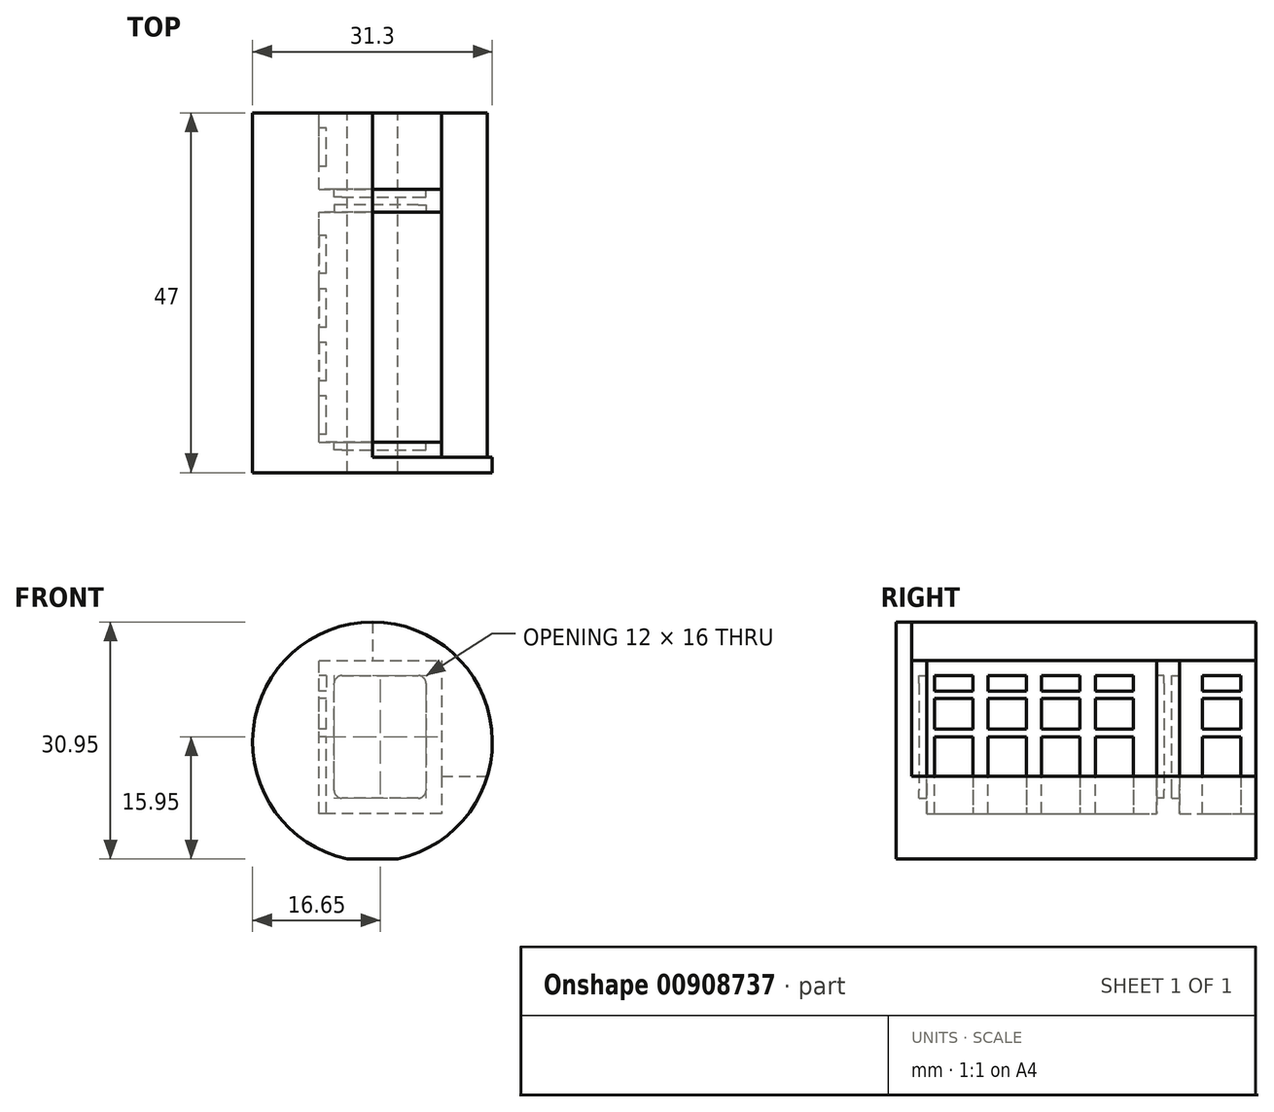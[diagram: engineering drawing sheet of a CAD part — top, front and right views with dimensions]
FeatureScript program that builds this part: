
annotation { "Feature Type Name" : "Feature", "Feature Type Description" : "" }
export const myFeature = defineFeature(function(context is Context, id is Id, definition is map)
    precondition{}
    {
        {
            var Q0;
            Q0=qCreatedBy(makeId("Front.planeOp"),FACE);
            var sketch = newSketch(context, id + "F0", { "sketchPlane" : qUnion([Q0])});
            skArc(sketch, "E0", {"start": v(3.3, 0) * mm, "mid": v(0, 30.95) * mm, "end": v(-3.3, 0) * mm});
            skLineSegment(sketch, "E1", {"start": v(3.3, 0) * mm, "end": v(-3.3, 0) * mm});
            skSolve(sketch);
        }
        {
            var Q0;
            Q0 = qSketchRegion(id + "F0", true);
            extrude(context, id + "F1", {"entities" : qUnion([Q0]), "depth" : 47 * mm, "offsetDistance" : 25 * mm});
        }
        {
            var Q0;
            Q0=makeQuery(id+"F1.opExtrude","CAP_FACE",FACE,{"disambiguationData":[OSD([sQuery(id+"F0.wireOp",EDGE,"E0"),sQuery(id+"F0.wireOp",EDGE,"E1")])],"isStart":true});
            var sketch = newSketch(context, id + "F2", { "sketchPlane" : qUnion([Q0])});
            skLineSegment(sketch, "E2", {"start": v(0, 30.95) * mm, "end": v(0, 25.95) * mm});
            skLineSegment(sketch, "E3", {"start": v(0, 25.95) * mm, "end": v(7, 25.95) * mm});
            skLineSegment(sketch, "E4", {"start": v(7, 25.95) * mm, "end": v(7, 5.95) * mm});
            skLineSegment(sketch, "E5", {"start": v(7, 5.95) * mm, "end": v(-9, 5.95) * mm});
            skLineSegment(sketch, "E6", {"start": v(-9, 5.95) * mm, "end": v(-9, 10.84) * mm});
            skLineSegment(sketch, "E7", {"start": v(-9, 10.84) * mm, "end": v(-15, 10.84) * mm});
            skArc(sketch, "E8.0", {"start": v(-15, 10.84) * mm, "mid": v(-12.55, 24.66) * mm, "end": v(0, 30.95) * mm});
            skPoint(sketch, "E9.orphan", {"position": v(3.3, 0) * mm});
            skPoint(sketch, "E10.orphan", {"position": v(-3.3, 0) * mm});
            skSolve(sketch);
        }
        {
            var Q0;
            Q0 = qSketchRegion(id + "F2", true);
            extrude(context, id + "F3", {"entities" : qUnion([Q0]), "operationType" : NewBodyOperationType.REMOVE, "oppositeDirection" : true, "depth" : 45 * mm, "offsetDistance" : 25 * mm});
        }
        {
            var Q0;
            Q0=makeQuery(id+"F3.boolean.opBoolean","COPY",FACE,{"derivedFrom":makeQuery(id+"F3.opExtrude","CAP_FACE",FACE,{"disambiguationData":[OSD([sQuery(id+"F2.wireOp",EDGE,"E2"),sQuery(id+"F2.wireOp",EDGE,"E3"),sQuery(id+"F2.wireOp",EDGE,"E4"),sQuery(id+"F2.wireOp",EDGE,"E5"),sQuery(id+"F2.wireOp",EDGE,"E6"),sQuery(id+"F2.wireOp",EDGE,"E7"),sQuery(id+"F2.wireOp",EDGE,"E8.0")])],"isStart":false})});
            var sketch = newSketch(context, id + "F4", { "sketchPlane" : qUnion([Q0])});
            skLineSegment(sketch, "E11", {"start": v(-9, 10.84) * mm, "end": v(-9, 25.95) * mm});
            skLineSegment(sketch, "E12", {"start": v(-9, 25.95) * mm, "end": v(0, 25.95) * mm});
            skLineSegment(sketch, "E13.0", {"start": v(7, 5.95) * mm, "end": v(-9, 5.95) * mm});
            skPoint(sketch, "E14.0", {"position": v(-9, 8.4) * mm});
            skLineSegment(sketch, "E15.0", {"start": v(-9, 5.95) * mm, "end": v(-9, 10.84) * mm});
            skLineSegment(sketch, "E16.0", {"start": v(0, 25.95) * mm, "end": v(7, 25.95) * mm});
            skLineSegment(sketch, "E17.0", {"start": v(7, 25.95) * mm, "end": v(7, 5.95) * mm});
            skSolve(sketch);
        }
        {
            var Q0;
            Q0=makeQuery(id+"F4.imprint","IMPRINT",FACE,{"disambiguationData":[TD([[makeQuery(id+"F4.imprint","IMPRINT",EDGE,{"derivedFrom":sQuery(id+"F4.wireOp",EDGE,"E11")}),-1.0]])]});
            extrude(context, id + "F5", {"entities" : qUnion([Q0]), "operationType" : NewBodyOperationType.ADD, "depth" : 2 * mm, "offsetDistance" : 25 * mm});
        }
        {
            var Q0;
            Q0=makeQuery(id+"F5.opExtrude","CAP_FACE",FACE,{"disambiguationData":[OSD([sQuery(id+"F4.wireOp",EDGE,"E11"),sQuery(id+"F4.wireOp",EDGE,"E12"),sQuery(id+"F4.wireOp",EDGE,"E13.0"),sQuery(id+"F4.wireOp",EDGE,"E15.0"),sQuery(id+"F4.wireOp",EDGE,"E16.0"),sQuery(id+"F4.wireOp",EDGE,"E17.0")])],"isStart":false});
            var sketch = newSketch(context, id + "F6", { "sketchPlane" : qUnion([Q0])});
            skLineSegment(sketch, "E18.0", {"start": v(-7, 23.95) * mm, "end": v(-7, 7.95) * mm});
            skLineSegment(sketch, "E18.1", {"start": v(0, 23.95) * mm, "end": v(-7, 23.95) * mm});
            skLineSegment(sketch, "E18.2", {"start": v(-7, 7.95) * mm, "end": v(5, 7.95) * mm});
            skLineSegment(sketch, "E18.3", {"start": v(5, 7.95) * mm, "end": v(5, 23.95) * mm});
            skLineSegment(sketch, "E18.4", {"start": v(5, 23.95) * mm, "end": v(0, 23.95) * mm});
            skSolve(sketch);
        }
        {
            var Q0;
            Q0 = qSketchRegion(id + "F6", true);
            extrude(context, id + "F7", {"entities" : qUnion([Q0]), "operationType" : NewBodyOperationType.REMOVE, "oppositeDirection" : true, "depth" : 1 * mm, "offsetDistance" : 25 * mm});
        }
        {
            var Q0;
            Q0=makeQuery(id+"F7.boolean.opBoolean","COPY",EDGE,{"derivedFrom":makeQuery(id+"F7.opExtrude","SWEPT_EDGE",EDGE,{"disambiguationData":[OSD([sQuery(id+"F6.wireOp",EDGE,"E18.0"),sQuery(id+"F6.wireOp",EDGE,"E18.1")])]})});
            var Q1;
            Q1=makeQuery(id+"F7.boolean.opBoolean","COPY",EDGE,{"derivedFrom":makeQuery(id+"F7.opExtrude","SWEPT_EDGE",EDGE,{"disambiguationData":[OSD([sQuery(id+"F6.wireOp",EDGE,"E18.3"),sQuery(id+"F6.wireOp",EDGE,"E18.4")])]})});
            var Q2;
            Q2=makeQuery(id+"F7.boolean.opBoolean","COPY",EDGE,{"derivedFrom":makeQuery(id+"F7.opExtrude","SWEPT_EDGE",EDGE,{"disambiguationData":[OSD([sQuery(id+"F6.wireOp",EDGE,"E18.0"),sQuery(id+"F6.wireOp",EDGE,"E18.2")])]})});
            var Q3;
            Q3=makeQuery(id+"F7.boolean.opBoolean","COPY",EDGE,{"derivedFrom":makeQuery(id+"F7.opExtrude","SWEPT_EDGE",EDGE,{"disambiguationData":[OSD([sQuery(id+"F6.wireOp",EDGE,"E18.2"),sQuery(id+"F6.wireOp",EDGE,"E18.3")])]})});
            fillet(context, id + "F8", {"entities" : qUnion([Q0, Q1, Q2, Q3]), "radius" : 1 * mm, "tangentPropagation" : true, "allowEdgeOverflow" : false});
        }
        {
            var Q0;
            Q0=makeQuery(id+"F3.boolean.opBoolean","COPY",FACE,{"derivedFrom":makeQuery(id+"F3.opExtrude","SWEPT_FACE",FACE,{"disambiguationData":[OSD([sQuery(id+"F2.wireOp",EDGE,"E4")])]})});
            var sketch = newSketch(context, id + "F9", { "sketchPlane" : qUnion([Q0])});
            skLineSegment(sketch, "E19", {"start": v(-42, 5.95) * mm, "end": v(-37, 5.95) * mm});
            skLineSegment(sketch, "E20", {"start": v(-42, 5.95) * mm, "end": v(-42, 15.95) * mm});
            skLineSegment(sketch, "E21", {"start": v(-42, 15.95) * mm, "end": v(-37, 15.95) * mm});
            skLineSegment(sketch, "E22", {"start": v(-37, 15.95) * mm, "end": v(-37, 5.95) * mm});
            skLineSegment(sketch, "E23.bottom", {"start": v(-42, 16.95) * mm, "end": v(-37, 16.95) * mm});
            skLineSegment(sketch, "E23.top", {"start": v(-42, 20.95) * mm, "end": v(-37, 20.95) * mm});
            skLineSegment(sketch, "E23.left", {"start": v(-42, 16.95) * mm, "end": v(-42, 20.95) * mm});
            skLineSegment(sketch, "E23.right", {"start": v(-37, 16.95) * mm, "end": v(-37, 20.95) * mm});
            skLineSegment(sketch, "E24", {"start": v(-42, 21.95) * mm, "end": v(-37, 21.95) * mm});
            skLineSegment(sketch, "E25", {"start": v(-37, 21.95) * mm, "end": v(-37, 23.95) * mm});
            skLineSegment(sketch, "E26", {"start": v(-37, 23.95) * mm, "end": v(-42, 23.95) * mm});
            skLineSegment(sketch, "E27", {"start": v(-42, 23.95) * mm, "end": v(-42, 21.95) * mm});
            skLineSegment(sketch, "E28.1.0.0", {"start": v(-30, 23.95) * mm, "end": v(-35, 23.95) * mm});
            skLineSegment(sketch, "E28.1.0.1", {"start": v(-35, 23.95) * mm, "end": v(-35, 21.95) * mm});
            skLineSegment(sketch, "E28.1.0.2", {"start": v(-35, 21.95) * mm, "end": v(-30, 21.95) * mm});
            skLineSegment(sketch, "E28.1.0.3", {"start": v(-30, 21.95) * mm, "end": v(-30, 23.95) * mm});
            skLineSegment(sketch, "E28.1.0.4", {"start": v(-35, 20.95) * mm, "end": v(-30, 20.95) * mm});
            skLineSegment(sketch, "E28.1.0.5", {"start": v(-35, 16.95) * mm, "end": v(-35, 20.95) * mm});
            skLineSegment(sketch, "E28.1.0.6", {"start": v(-30, 16.95) * mm, "end": v(-30, 20.95) * mm});
            skLineSegment(sketch, "E28.1.0.7", {"start": v(-35, 16.95) * mm, "end": v(-30, 16.95) * mm});
            skLineSegment(sketch, "E28.1.0.8", {"start": v(-35, 15.95) * mm, "end": v(-30, 15.95) * mm});
            skLineSegment(sketch, "E28.1.0.9", {"start": v(-35, 5.95) * mm, "end": v(-35, 15.95) * mm});
            skLineSegment(sketch, "E28.1.0.10", {"start": v(-35, 5.95) * mm, "end": v(-30, 5.95) * mm});
            skLineSegment(sketch, "E28.1.0.11", {"start": v(-30, 15.95) * mm, "end": v(-30, 5.95) * mm});
            skLineSegment(sketch, "E28.2.0.0", {"start": v(-23, 23.95) * mm, "end": v(-28, 23.95) * mm});
            skLineSegment(sketch, "E28.2.0.1", {"start": v(-28, 23.95) * mm, "end": v(-28, 21.95) * mm});
            skLineSegment(sketch, "E28.2.0.2", {"start": v(-28, 21.95) * mm, "end": v(-23, 21.95) * mm});
            skLineSegment(sketch, "E28.2.0.3", {"start": v(-23, 21.95) * mm, "end": v(-23, 23.95) * mm});
            skLineSegment(sketch, "E28.2.0.4", {"start": v(-28, 20.95) * mm, "end": v(-23, 20.95) * mm});
            skLineSegment(sketch, "E28.2.0.5", {"start": v(-28, 16.95) * mm, "end": v(-28, 20.95) * mm});
            skLineSegment(sketch, "E28.2.0.6", {"start": v(-23, 16.95) * mm, "end": v(-23, 20.95) * mm});
            skLineSegment(sketch, "E28.2.0.7", {"start": v(-28, 16.95) * mm, "end": v(-23, 16.95) * mm});
            skLineSegment(sketch, "E28.2.0.8", {"start": v(-28, 15.95) * mm, "end": v(-23, 15.95) * mm});
            skLineSegment(sketch, "E28.2.0.9", {"start": v(-28, 5.95) * mm, "end": v(-28, 15.95) * mm});
            skLineSegment(sketch, "E28.2.0.10", {"start": v(-28, 5.95) * mm, "end": v(-23, 5.95) * mm});
            skLineSegment(sketch, "E28.2.0.11", {"start": v(-23, 15.95) * mm, "end": v(-23, 5.95) * mm});
            skLineSegment(sketch, "E28.3.0.0", {"start": v(-16, 23.95) * mm, "end": v(-21, 23.95) * mm});
            skLineSegment(sketch, "E28.3.0.1", {"start": v(-21, 23.95) * mm, "end": v(-21, 21.95) * mm});
            skLineSegment(sketch, "E28.3.0.2", {"start": v(-21, 21.95) * mm, "end": v(-16, 21.95) * mm});
            skLineSegment(sketch, "E28.3.0.3", {"start": v(-16, 21.95) * mm, "end": v(-16, 23.95) * mm});
            skLineSegment(sketch, "E28.3.0.4", {"start": v(-21, 20.95) * mm, "end": v(-16, 20.95) * mm});
            skLineSegment(sketch, "E28.3.0.5", {"start": v(-21, 16.95) * mm, "end": v(-21, 20.95) * mm});
            skLineSegment(sketch, "E28.3.0.6", {"start": v(-16, 16.95) * mm, "end": v(-16, 20.95) * mm});
            skLineSegment(sketch, "E28.3.0.7", {"start": v(-21, 16.95) * mm, "end": v(-16, 16.95) * mm});
            skLineSegment(sketch, "E28.3.0.8", {"start": v(-21, 15.95) * mm, "end": v(-16, 15.95) * mm});
            skLineSegment(sketch, "E28.3.0.9", {"start": v(-21, 5.95) * mm, "end": v(-21, 15.95) * mm});
            skLineSegment(sketch, "E28.3.0.10", {"start": v(-21, 5.95) * mm, "end": v(-16, 5.95) * mm});
            skLineSegment(sketch, "E28.3.0.11", {"start": v(-16, 15.95) * mm, "end": v(-16, 5.95) * mm});
            skLineSegment(sketch, "E28.direction1", {"start": v(-42, 23.95) * mm, "end": v(-35, 23.95) * mm, "construction": true});
            skLineSegment(sketch, "E29.1.0.0", {"start": v(-7, 21.95) * mm, "end": v(-2, 21.95) * mm});
            skLineSegment(sketch, "E29.1.0.1", {"start": v(-2, 23.95) * mm, "end": v(-7, 23.95) * mm});
            skLineSegment(sketch, "E29.1.0.2", {"start": v(-7, 23.95) * mm, "end": v(-7, 21.95) * mm});
            skLineSegment(sketch, "E29.1.0.3", {"start": v(-2, 21.95) * mm, "end": v(-2, 23.95) * mm});
            skLineSegment(sketch, "E29.1.0.4", {"start": v(-7, 20.95) * mm, "end": v(-2, 20.95) * mm});
            skLineSegment(sketch, "E29.1.0.5", {"start": v(-7, 16.95) * mm, "end": v(-7, 20.95) * mm});
            skLineSegment(sketch, "E29.1.0.6", {"start": v(-7, 16.95) * mm, "end": v(-2, 16.95) * mm});
            skLineSegment(sketch, "E29.1.0.7", {"start": v(-2, 16.95) * mm, "end": v(-2, 20.95) * mm});
            skLineSegment(sketch, "E29.1.0.8", {"start": v(-7, 15.95) * mm, "end": v(-2, 15.95) * mm});
            skLineSegment(sketch, "E29.1.0.9", {"start": v(-7, 5.95) * mm, "end": v(-7, 15.95) * mm});
            skLineSegment(sketch, "E29.1.0.10", {"start": v(-7, 5.95) * mm, "end": v(-2, 5.95) * mm});
            skLineSegment(sketch, "E29.1.0.11", {"start": v(-2, 15.95) * mm, "end": v(-2, 5.95) * mm});
            skLineSegment(sketch, "E29.direction1", {"start": v(-21, 21.95) * mm, "end": v(-7, 21.95) * mm, "construction": true});
            skSolve(sketch);
        }
        {
            var Q0;
            Q0 = qSketchRegion(id + "F9", true);
            extrude(context, id + "F10", {"entities" : qUnion([Q0]), "operationType" : NewBodyOperationType.ADD, "depth" : 1 * mm, "offsetDistance" : 25 * mm});
        }
        {
            var Q0;
            Q0=makeQuery(id+"F5.opExtrude","CAP_FACE",FACE,{"disambiguationData":[OSD([sQuery(id+"F4.wireOp",EDGE,"E11"),sQuery(id+"F4.wireOp",EDGE,"E12"),sQuery(id+"F4.wireOp",EDGE,"E13.0"),sQuery(id+"F4.wireOp",EDGE,"E15.0"),sQuery(id+"F4.wireOp",EDGE,"E16.0"),sQuery(id+"F4.wireOp",EDGE,"E17.0")])],"isStart":false});
            cPlane(context, id + "F11", {"entities" : qUnion([Q0]), "cplaneType" : CPlaneType.OFFSET, "offset" : 30 * mm, "width" : 150 * mm, "height" : 150 * mm});
        }
        {
            var Q0;
            Q0=qCreatedBy(id+"F11.planeOp",FACE);
            var sketch = newSketch(context, id + "F12", { "sketchPlane" : qUnion([Q0])});
            skLineSegment(sketch, "E30.0.0", {"start": v(0, 25.95) * mm, "end": v(-9, 25.95) * mm});
            skLineSegment(sketch, "E30.0.1", {"start": v(-9, 25.95) * mm, "end": v(-9, 10.84) * mm});
            skLineSegment(sketch, "E30.0.2", {"start": v(-9, 10.84) * mm, "end": v(-9, 5.95) * mm});
            skLineSegment(sketch, "E30.0.3", {"start": v(-9, 5.95) * mm, "end": v(7, 5.95) * mm});
            skLineSegment(sketch, "E30.0.4", {"start": v(7, 5.95) * mm, "end": v(7, 25.95) * mm});
            skLineSegment(sketch, "E30.0.5", {"start": v(7, 25.95) * mm, "end": v(0, 25.95) * mm});
            skSolve(sketch);
        }
        {
            var Q0;
            Q0 = qSketchRegion(id + "F12", true);
            extrude(context, id + "F13", {"entities" : qUnion([Q0]), "operationType" : NewBodyOperationType.ADD, "depth" : 3 * mm, "offsetDistance" : 25 * mm});
        }
        {
            var Q0;
            Q0=makeQuery(id+"F13.opExtrude","CAP_FACE",FACE,{"disambiguationData":[OSD([sQuery(id+"F12.wireOp",EDGE,"E30.0.0"),sQuery(id+"F12.wireOp",EDGE,"E30.0.1"),sQuery(id+"F12.wireOp",EDGE,"E30.0.2"),sQuery(id+"F12.wireOp",EDGE,"E30.0.3"),sQuery(id+"F12.wireOp",EDGE,"E30.0.4"),sQuery(id+"F12.wireOp",EDGE,"E30.0.5")])],"isStart":false});
            var sketch = newSketch(context, id + "F14", { "sketchPlane" : qUnion([Q0])});
            skLineSegment(sketch, "E31.0.0", {"start": v(5, 8.95) * mm, "end": v(5, 22.95) * mm});
            skArc(sketch, "E31.0.1", {"start": v(5, 22.95) * mm, "mid": v(4.7, 23.66) * mm, "end": v(4, 23.95) * mm});
            skLineSegment(sketch, "E31.0.2", {"start": v(4, 23.95) * mm, "end": v(-6, 23.95) * mm});
            skArc(sketch, "E31.0.3", {"start": v(-6, 23.95) * mm, "mid": v(-6.7, 23.66) * mm, "end": v(-7, 22.95) * mm});
            skLineSegment(sketch, "E31.0.4", {"start": v(-7, 22.95) * mm, "end": v(-7, 8.95) * mm});
            skArc(sketch, "E31.0.5", {"start": v(-7, 8.95) * mm, "mid": v(-6.7, 8.24) * mm, "end": v(-6, 7.95) * mm});
            skLineSegment(sketch, "E31.0.6", {"start": v(-6, 7.95) * mm, "end": v(4, 7.95) * mm});
            skArc(sketch, "E31.0.7", {"start": v(4, 7.95) * mm, "mid": v(4.7, 8.24) * mm, "end": v(5, 8.95) * mm});
            skSolve(sketch);
        }
        {
            var Q0;
            Q0 = qSketchRegion(id + "F14", true);
            extrude(context, id + "F15", {"entities" : qUnion([Q0]), "operationType" : NewBodyOperationType.REMOVE, "oppositeDirection" : true, "depth" : 1 * mm, "offsetDistance" : 25 * mm});
        }
        {
            var Q0;
            Q0=makeQuery(id+"F13.opExtrude","CAP_FACE",FACE,{"disambiguationData":[OSD([sQuery(id+"F12.wireOp",EDGE,"E30.0.0"),sQuery(id+"F12.wireOp",EDGE,"E30.0.1"),sQuery(id+"F12.wireOp",EDGE,"E30.0.2"),sQuery(id+"F12.wireOp",EDGE,"E30.0.3"),sQuery(id+"F12.wireOp",EDGE,"E30.0.4"),sQuery(id+"F12.wireOp",EDGE,"E30.0.5")])],"isStart":true});
            var sketch = newSketch(context, id + "F16", { "sketchPlane" : qUnion([Q0])});
            skLineSegment(sketch, "E32.0.0", {"start": v(6, 7.95) * mm, "end": v(-4, 7.95) * mm});
            skArc(sketch, "E32.0.1", {"start": v(-4, 7.95) * mm, "mid": v(-4.7, 8.24) * mm, "end": v(-5, 8.95) * mm});
            skLineSegment(sketch, "E32.0.2", {"start": v(-5, 8.95) * mm, "end": v(-5, 22.95) * mm});
            skArc(sketch, "E32.0.3", {"start": v(-5, 22.95) * mm, "mid": v(-4.7, 23.66) * mm, "end": v(-4, 23.95) * mm});
            skLineSegment(sketch, "E32.0.4", {"start": v(-4, 23.95) * mm, "end": v(6, 23.95) * mm});
            skArc(sketch, "E32.0.5", {"start": v(6, 23.95) * mm, "mid": v(6.7, 23.66) * mm, "end": v(7, 22.95) * mm});
            skLineSegment(sketch, "E32.0.6", {"start": v(7, 22.95) * mm, "end": v(7, 8.95) * mm});
            skArc(sketch, "E32.0.7", {"start": v(7, 8.95) * mm, "mid": v(6.7, 8.24) * mm, "end": v(6, 7.95) * mm});
            skSolve(sketch);
        }
        {
            var Q0;
            Q0 = qSketchRegion(id + "F16", true);
            extrude(context, id + "F17", {"entities" : qUnion([Q0]), "operationType" : NewBodyOperationType.REMOVE, "oppositeDirection" : true, "depth" : 1 * mm, "offsetDistance" : 25 * mm});
        }
    });
